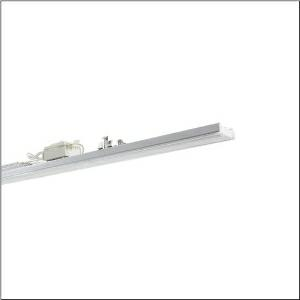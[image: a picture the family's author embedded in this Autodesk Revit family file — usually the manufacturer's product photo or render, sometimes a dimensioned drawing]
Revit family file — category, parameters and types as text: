
# Revit family: licross_r__11_recessed_mo_51tl10mn4axg_479a
name_source: partatom
category: Lighting Fixtures
units: mm (PartAtom-declared; Revit-internal decimal feet)

## family parameters
Cut with Voids When Loaded = No
Host = Face
Light Source = No
Part Type = Normal
Room Calculation Point = No
Round Connector Dimension = Use Diameter
Shared = No

## types (1)
- --- (1 x LED, 10000 lm, 55.2 W, 4000K)
    Apparent Load = 55 VA
    CIE Flux Codes = 50 81 96 100 100
    Color Rendering = 80
    Color Temperature = 4000K
    Default Elevation = 1800 mm
    Description = Licross® 11 Recessed MO, luminaire insert, of sheet steel, coil coated, white, length: 1.500mm, width: 66mm, height: 67mm, LED rated luminous flux: 10.000lm, light colour: 840, control gear: ON/OFF Multilumen, with plug, 3-pole, with phase selection, mains connection: 220..240V, AC, 50/60Hz, rated input power: 55W, halogen-free wiring, primary optical cover: cover, of PMMA, light emission: direct distribution, primary light characteristic: symmetric, protection rating (complete): IP40, insulation class (complete): insulation class I (protective earthing), certification: CE, ENEC, VDE, UKCA, protection symbol: D if used in an environment without relevant dust loads with corresponding accessories, impact resistance: IK06, permissible ambient temperature for indoor applications: -35..+40°C, corresponds to IFS (International Featured Standards) requirements for safety and quality in the food industry, reducing of maximum allowable ambient temperature of 5°C with ceiling mounting, packaging unit: 1 piece
    Height = 58 mm
    Lamp = 1 x LED
    Lamp Light Flux = 10000 lm
    Lamp Power = 55.2 W
    Lamp count = 1
    Length = 1500 mm
    Luminous efficacy = 181 lm/W
    Manufacturer = Siteco
    ModVariant = No
    Model = 51TL10MN4AXG
    Mounting Place = Ceiling
    Mounting Type = Pendant
    Number of Poles = 1
    OnlyDefault = Yes
    Power Factor = 1
    Product Name = Licross® 11 Recessed MO
    Product group = luminaire insert
    ProductGroupID = 902
    Protection Class = Protection class I
    Protection Degree = IP 40
    RLX_Detail_Level = 1
    RLX_Emergency_Light_Flux = 0 lm
    RLX_Emergency_Type = 0
    RLX_Emergency_Type_DB = No
    RlxData = <blob elided: 22069 chars, md5=855b4ed3>
    Socket = socket
    Standby Power = 0 W
    System Light Flux = 10000 lm
    System Power = 55 W
    Type Comments = factory setting: luminous flux: 100 % | (A | C | E) | 126 mA
    Type Image = l_1296930.jpg
    URL = http://relux.com
    VarID = @adj_085190
    Voltage = 0 V
    Weight = 0.00 kg
    Width = 66 mm

## geometry (parser evidence)
native form markers: Blend x4, Sweep x11
no freeform markers — native parametric forms only
